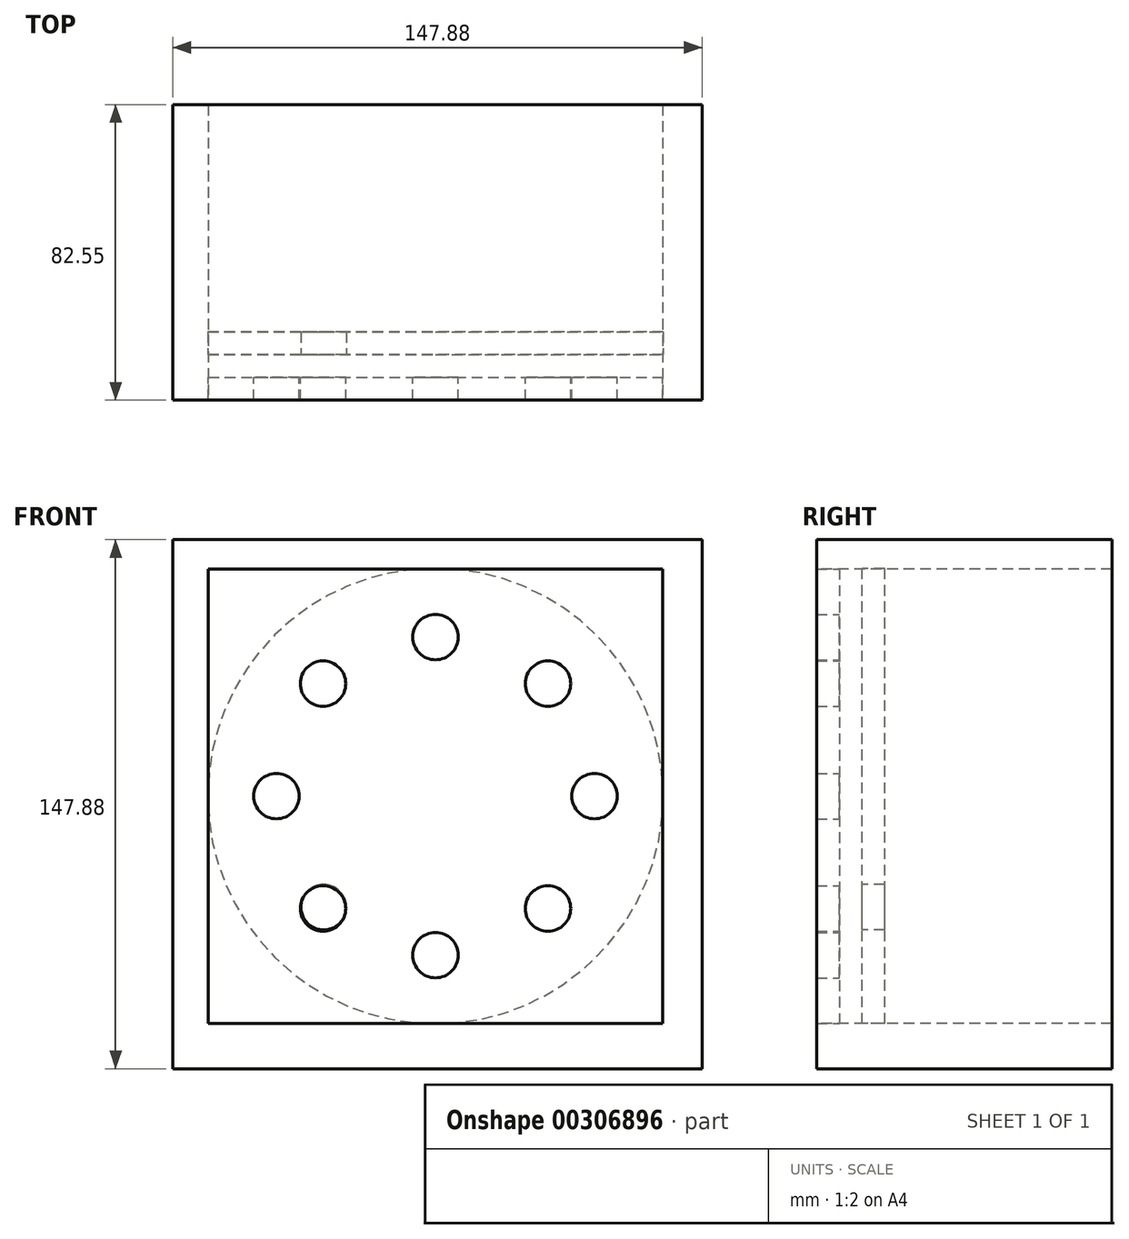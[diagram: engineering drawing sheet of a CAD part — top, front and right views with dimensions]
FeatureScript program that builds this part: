
annotation { "Feature Type Name" : "Feature", "Feature Type Description" : "" }
export const myFeature = defineFeature(function(context is Context, id is Id, definition is map)
    precondition{}
    {
        {
            var Q0;
            Q0=qCreatedBy(makeId("Front.planeOp"),FACE);
            var sketch = newSketch(context, id + "F0", { "sketchPlane" : qUnion([Q0])});
            skLineSegment(sketch, "E0.bottom", {"start": v(-63.5, 63.5) * mm, "end": v(63.5, 63.5) * mm});
            skLineSegment(sketch, "E0.top", {"start": v(-63.5, -63.5) * mm, "end": v(63.5, -63.5) * mm});
            skLineSegment(sketch, "E0.left", {"start": v(-63.5, 63.5) * mm, "end": v(-63.5, -63.5) * mm});
            skLineSegment(sketch, "E0.right", {"start": v(63.5, 63.5) * mm, "end": v(63.5, -63.5) * mm});
            skLineSegment(sketch, "E1", {"start": v(-63.5, 0) * mm, "end": v(0, 0) * mm, "construction": true});
            skLineSegment(sketch, "E2", {"start": v(0, 0) * mm, "end": v(63.5, 0) * mm, "construction": true});
            skCircle(sketch, "E3", {"center": v(0, 0) * mm, "radius": 44.45 * mm});
            skCircle(sketch, "E4", {"center": v(0, 44.45) * mm, "radius": 6.35 * mm});
            skCircle(sketch, "E5.1.0", {"center": v(-31.43, 31.43) * mm, "radius": 6.35 * mm});
            skCircle(sketch, "E5.2.0", {"center": v(-44.45, 0) * mm, "radius": 6.35 * mm});
            skCircle(sketch, "E5.3.0", {"center": v(-31.43, -31.43) * mm, "radius": 6.35 * mm});
            skCircle(sketch, "E5.4.0", {"center": v(0, -44.45) * mm, "radius": 6.35 * mm});
            skCircle(sketch, "E5.5.0", {"center": v(31.43, -31.43) * mm, "radius": 6.35 * mm});
            skCircle(sketch, "E5.6.0", {"center": v(44.45, 0) * mm, "radius": 6.35 * mm});
            skCircle(sketch, "E5.7.0", {"center": v(31.43, 31.43) * mm, "radius": 6.35 * mm});
            skSolve(sketch);
        }
        {
            var Q0;
            Q0=makeQuery(id+"F0.imprint","IMPRINT",FACE,{"disambiguationData":[TD([[makeQuery(id+"F0.imprint","IMPRINT",EDGE,{"derivedFrom":sQuery(id+"F0.wireOp",EDGE,"E0.bottom")}),-1.0]])]});
            var Q1;
            {var subQ0=sQuery(id+"F0.wireOp",EDGE,"E3");var subQ13=sQuery(id+"F0.wireOp",EDGE,"E4");var subQ14=makeQuery(id+"F0.imprint","INTERSECT",VERTEX,{"disambiguationData":[OD(0.0)],"derivedFrom":[subQ13,subQ0]});Q1=makeQuery(id+"F0.imprint","IMPRINT",FACE,{"disambiguationData":[TD([[makeQuery(id+"F0.imprint","IMPRINT",EDGE,{"disambiguationData":[TD([[subQ14,1.0]])],"derivedFrom":subQ13}),-1.0]])]});}
            extrude(context, id + "F1", {"entities" : qUnion([Q0, Q1]), "depth" : 6.35 * mm});
        }
        {
            var Q0;
            Q0=qCreatedBy(makeId("Front.planeOp"),FACE);
            cPlane(context, id + "F2", {"entities" : qUnion([Q0]), "cplaneType" : CPlaneType.OFFSET, "offset" : 6.35 * mm, "oppositeDirection" : true, "width" : 152.4 * mm, "height" : 152.4 * mm});
        }
        {
            var Q0;
            Q0=qCreatedBy(id+"F2.planeOp",FACE);
            var sketch = newSketch(context, id + "F3", { "sketchPlane" : qUnion([Q0])});
            skCircle(sketch, "E6.3.0", {"center": v(-31.25, -31.06) * mm, "radius": 6.35 * mm});
            skCircle(sketch, "E7", {"center": v(0, 0) * mm, "radius": 63.6 * mm});
            skSolve(sketch);
        }
        {
            var Q0;
            Q0=makeQuery(id+"F3.imprint","IMPRINT",FACE,{"disambiguationData":[TD([[makeQuery(id+"F3.imprint","IMPRINT",EDGE,{"derivedFrom":sQuery(id+"F3.wireOp",EDGE,"E6.3.0")}),-1.0]])]});
            extrude(context, id + "F4", {"entities" : qUnion([Q0]), "oppositeDirection" : true, "depth" : 6.35 * mm});
        }
        {
            var Q0;
            Q0=qCreatedBy(makeId("Front.planeOp"),FACE);
            var sketch = newSketch(context, id + "F5", { "sketchPlane" : qUnion([Q0])});
            skLineSegment(sketch, "E8.bottom", {"start": v(-63.5, 63.5) * mm, "end": v(63.5, 63.5) * mm});
            skLineSegment(sketch, "E8.top", {"start": v(-63.5, -63.5) * mm, "end": v(63.5, -63.5) * mm});
            skLineSegment(sketch, "E8.left", {"start": v(-63.5, 63.5) * mm, "end": v(-63.5, -63.5) * mm});
            skLineSegment(sketch, "E8.right", {"start": v(63.5, 63.5) * mm, "end": v(63.5, -63.5) * mm});
            skLineSegment(sketch, "E9.bottom", {"start": v(-73.38, 71.68) * mm, "end": v(74.5, 71.68) * mm});
            skLineSegment(sketch, "E9.top", {"start": v(-73.38, -76.2) * mm, "end": v(74.5, -76.2) * mm});
            skLineSegment(sketch, "E9.left", {"start": v(-73.38, 71.68) * mm, "end": v(-73.38, -76.2) * mm});
            skLineSegment(sketch, "E9.right", {"start": v(74.5, 71.68) * mm, "end": v(74.5, -76.2) * mm});
            skLineSegment(sketch, "E10", {"start": v(0, -63.5) * mm, "end": v(0, -76.2) * mm, "construction": true});
            skSolve(sketch);
        }
        {
            var Q0;
            Q0 = qSketchRegion(id + "F5", true);
            extrude(context, id + "F6", {"entities" : qUnion([Q0]), "oppositeDirection" : true, "depth" : 76.2 * mm, "hasSecondDirection" : true, "secondDirectionOppositeDirection" : false, "secondDirectionDepth" : 6.35 * mm});
        }
    });
